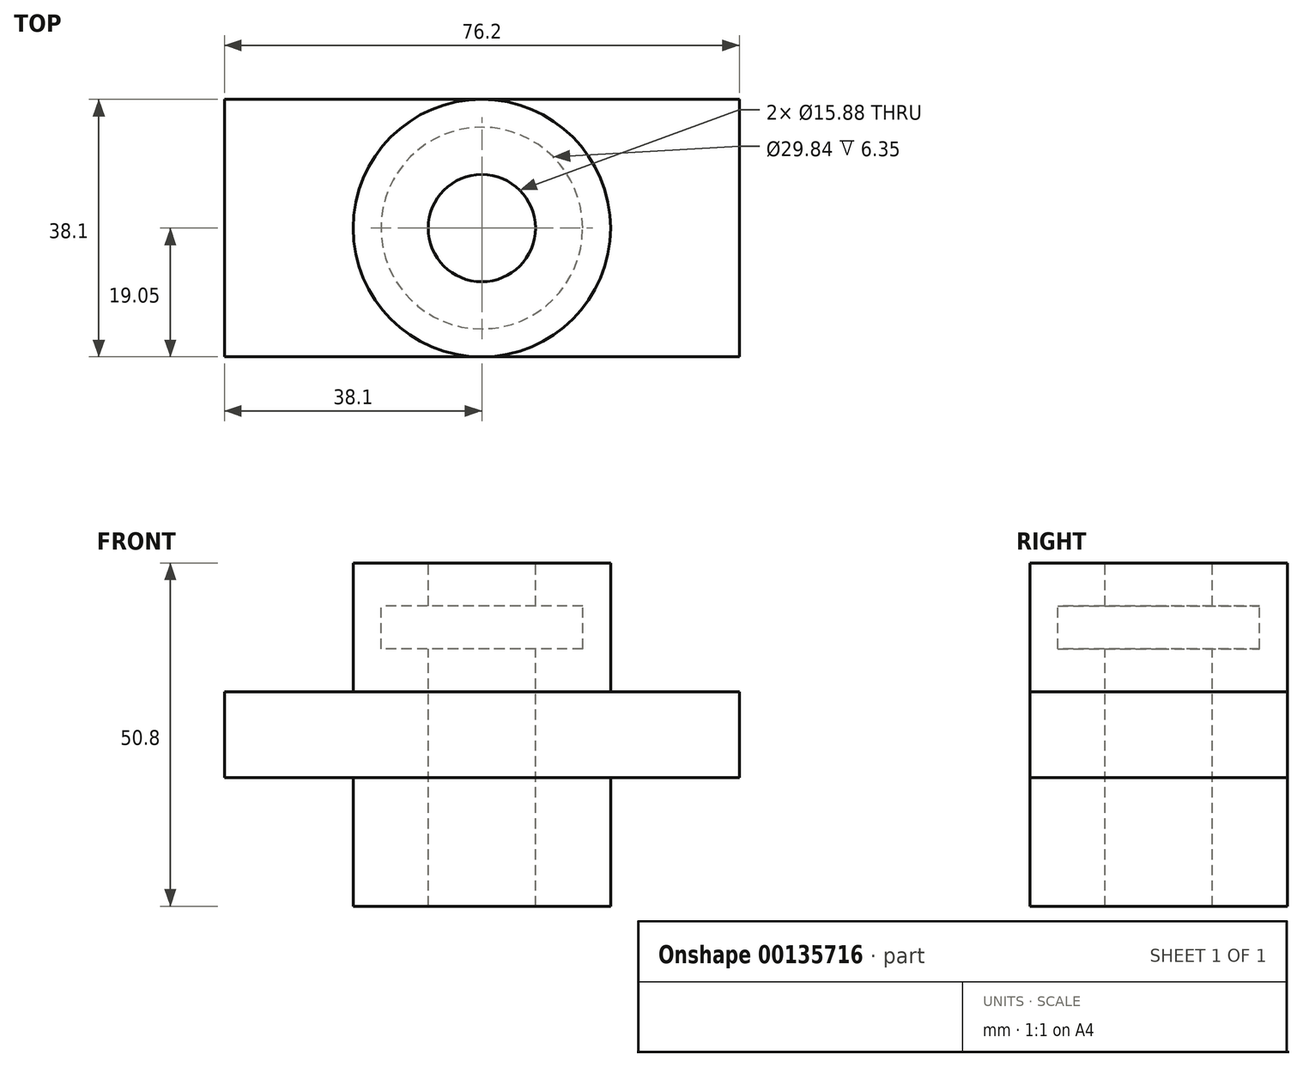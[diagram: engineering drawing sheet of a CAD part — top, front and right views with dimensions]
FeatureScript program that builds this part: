
annotation { "Feature Type Name" : "Feature", "Feature Type Description" : "" }
export const myFeature = defineFeature(function(context is Context, id is Id, definition is map)
    precondition{}
    {
        {
            var Q0;
            Q0=qCreatedBy(makeId("Top.planeOp"),FACE);
            var sketch = newSketch(context, id + "F0", { "sketchPlane" : qUnion([Q0])});
            skLineSegment(sketch, "E0.bottom", {"start": v(0, 0) * mm, "end": v(76.2, 0) * mm});
            skLineSegment(sketch, "E0.top", {"start": v(0, 38.1) * mm, "end": v(76.2, 38.1) * mm});
            skLineSegment(sketch, "E0.left", {"start": v(0, 0) * mm, "end": v(0, 38.1) * mm});
            skLineSegment(sketch, "E0.right", {"start": v(76.2, 0) * mm, "end": v(76.2, 38.1) * mm});
            skSolve(sketch);
        }
        {
            var Q0;
            Q0 = qSketchRegion(id + "F0", true);
            extrude(context, id + "F1", {"entities" : qUnion([Q0]), "depth" : 12.7 * mm});
        }
        {
            var Q0;
            Q0=makeQuery(id+"F1.opExtrude","CAP_FACE",FACE,{"disambiguationData":[OSD([sQuery(id+"F0.wireOp",EDGE,"E0.bottom"),sQuery(id+"F0.wireOp",EDGE,"E0.top"),sQuery(id+"F0.wireOp",EDGE,"E0.left"),sQuery(id+"F0.wireOp",EDGE,"E0.right")])],"isStart":false});
            var sketch = newSketch(context, id + "F2", { "sketchPlane" : qUnion([Q0])});
            skCircle(sketch, "E1", {"center": v(38.1, 19.05) * mm, "radius": 19.05 * mm});
            skSolve(sketch);
        }
        {
            var Q0;
            Q0 = qSketchRegion(id + "F2", true);
            extrude(context, id + "F3", {"entities" : qUnion([Q0]), "operationType" : NewBodyOperationType.ADD, "depth" : 19.05 * mm});
        }
        {
            var Q0;
            Q0=makeQuery(id+"F1.opExtrude","CAP_FACE",FACE,{"disambiguationData":[OSD([sQuery(id+"F0.wireOp",EDGE,"E0.bottom"),sQuery(id+"F0.wireOp",EDGE,"E0.top"),sQuery(id+"F0.wireOp",EDGE,"E0.left"),sQuery(id+"F0.wireOp",EDGE,"E0.right")])],"isStart":true});
            var sketch = newSketch(context, id + "F4", { "sketchPlane" : qUnion([Q0])});
            skCircle(sketch, "E2", {"center": v(38.1, -19.05) * mm, "radius": 19.05 * mm});
            skPoint(sketch, "E2.centerSnap0", {"position": v(38.1, -38.1) * mm});
            skSolve(sketch);
        }
        {
            var Q0;
            Q0 = qSketchRegion(id + "F4", true);
            extrude(context, id + "F5", {"entities" : qUnion([Q0]), "operationType" : NewBodyOperationType.ADD, "depth" : 19.05 * mm});
        }
        {
            var Q0;
            Q0=qCreatedBy(makeId("Top.planeOp"),FACE);
            var sketch = newSketch(context, id + "F6", { "sketchPlane" : qUnion([Q0])});
            skCircle(sketch, "E3", {"center": v(38.1, 19.05) * mm, "radius": 7.94 * mm});
            skSolve(sketch);
        }
        {
            var Q0;
            Q0 = qSketchRegion(id + "F6", true);
            extrude(context, id + "F7", {"entities" : qUnion([Q0]), "operationType" : NewBodyOperationType.REMOVE, "endBound" : BoundingType.THROUGH_ALL, "oppositeDirection" : true, "depth" : 25.4 * mm, "hasSecondDirection" : true, "secondDirectionBound" : SecondDirectionBoundingType.THROUGH_ALL, "secondDirectionOppositeDirection" : false, "secondDirectionDepth" : 25.4 * mm});
        }
        {
            var Q0;
            Q0=makeQuery(id+"F3.opExtrude","CAP_FACE",FACE,{"disambiguationData":[OSD([sQuery(id+"F2.wireOp",EDGE,"E1")])],"isStart":false});
            var sketch = newSketch(context, id + "F8", { "sketchPlane" : qUnion([Q0])});
            skCircle(sketch, "E4", {"center": v(38.1, 19.05) * mm, "radius": 14.92 * mm});
            skSolve(sketch);
        }
        {
            var Q0;
            Q0=makeQuery(id+"F8.imprint","IMPRINT",FACE,{"disambiguationData":[TD([[makeQuery(id+"F8.imprint","IMPRINT",EDGE,{"derivedFrom":sQuery(id+"F8.wireOp",EDGE,"E4")}),1.0]])]});
            extrude(context, id + "F9", {"entities" : qUnion([Q0]), "operationType" : NewBodyOperationType.REMOVE, "oppositeDirection" : true, "depth" : 12.7 * mm, "hasSecondDirection" : true, "secondDirectionOppositeDirection" : true, "secondDirectionDepth" : 6.35 * mm});
        }
    });
